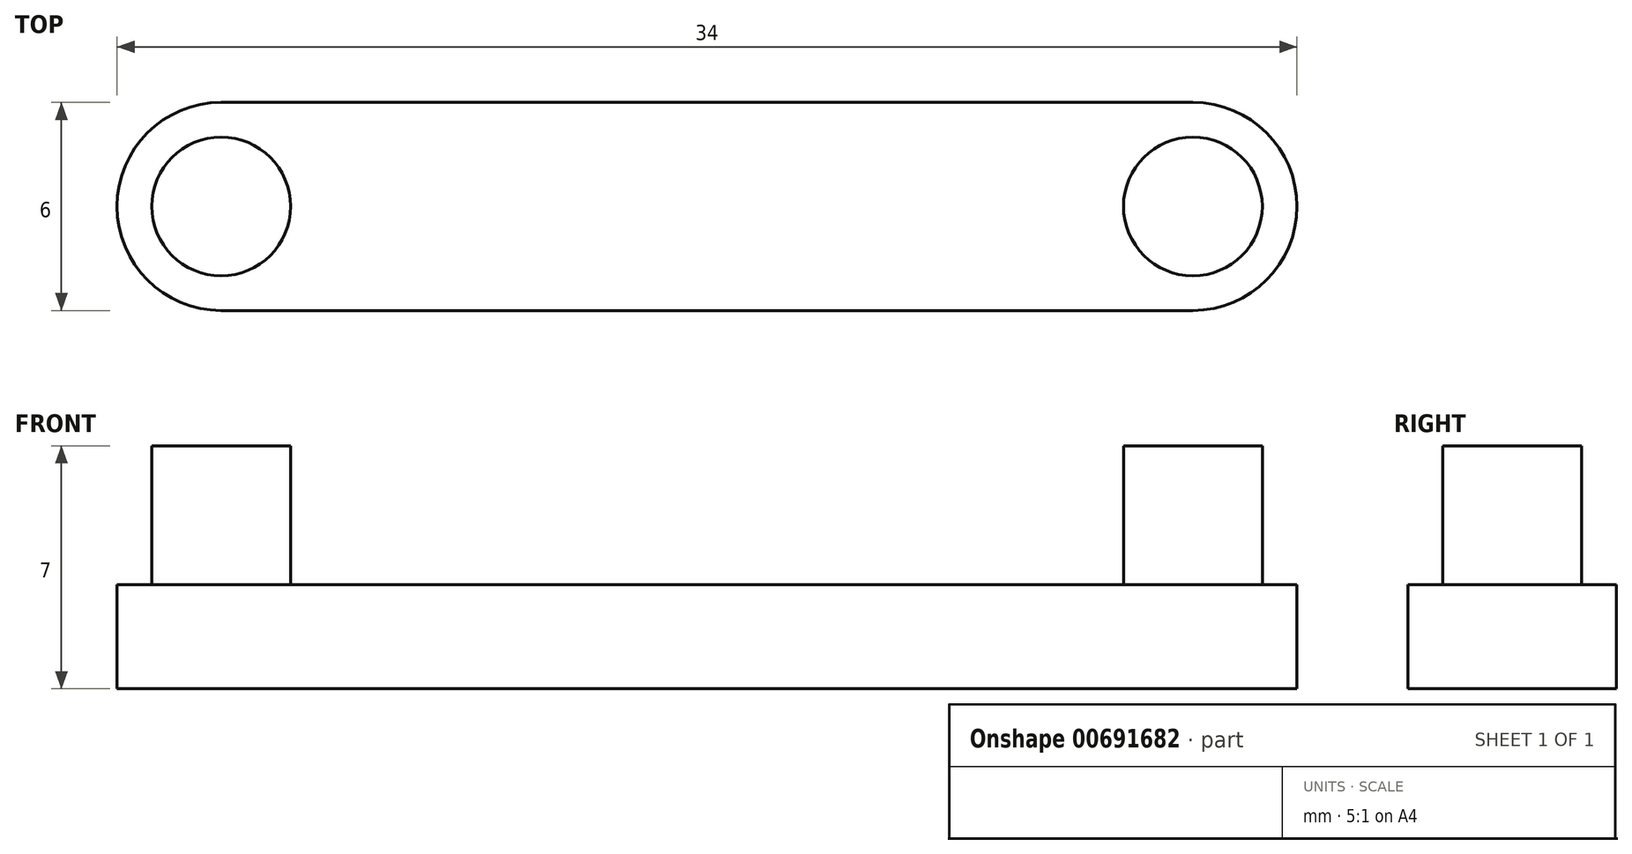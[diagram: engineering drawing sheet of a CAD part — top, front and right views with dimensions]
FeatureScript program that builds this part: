
annotation { "Feature Type Name" : "Feature", "Feature Type Description" : "" }
export const myFeature = defineFeature(function(context is Context, id is Id, definition is map)
    precondition{}
    {
        {
            var Q0;
            Q0=qCreatedBy(makeId("Top.planeOp"),FACE);
            var sketch = newSketch(context, id + "F0", { "sketchPlane" : qUnion([Q0])});
            skLineSegment(sketch, "E0.bottom", {"start": v(2, 3) * mm, "end": v(-2, 3) * mm});
            skLineSegment(sketch, "E0.top", {"start": v(2, -3) * mm, "end": v(-2, -3) * mm});
            skLineSegment(sketch, "E0.left", {"start": v(2, 3) * mm, "end": v(2, -3) * mm});
            skLineSegment(sketch, "E0.right", {"start": v(-2, 3) * mm, "end": v(-2, -3) * mm});
            skPoint(sketch, "E0.middle", {"position": v(0, 0) * mm});
            skLineSegment(sketch, "E1.bottom", {"start": v(2, 3) * mm, "end": v(14, 3) * mm});
            skLineSegment(sketch, "E1.top", {"start": v(2, -3) * mm, "end": v(14, -3) * mm});
            skLineSegment(sketch, "E1.right", {"start": v(14, 3) * mm, "end": v(14, -3) * mm});
            skLineSegment(sketch, "E2.bottom", {"start": v(-2, 3) * mm, "end": v(-14, 3) * mm});
            skLineSegment(sketch, "E2.top", {"start": v(-2, -3) * mm, "end": v(-14, -3) * mm});
            skLineSegment(sketch, "E2.right", {"start": v(-14, 3) * mm, "end": v(-14, -3) * mm});
            skCircle(sketch, "E3", {"center": v(14, 0) * mm, "radius": 3 * mm});
            skCircle(sketch, "E4", {"center": v(-14, 0) * mm, "radius": 3 * mm});
            skCircle(sketch, "E5", {"center": v(-14, 0) * mm, "radius": 2 * mm});
            skCircle(sketch, "E6", {"center": v(14, 0) * mm, "radius": 2 * mm});
            skSolve(sketch);
        }
        {
            var Q0;
            Q0 = qSketchRegion(id + "F0", true);
            extrude(context, id + "F1", {"entities" : qUnion([Q0]), "depth" : 3 * mm, "offsetDistance" : 25 * mm});
        }
        {
            var Q0;
            {var subQ0=sQuery(id+"F0.wireOp",EDGE,"E6");var subQ1=sQuery(id+"F0.wireOp",EDGE,"E1.right");var subQ2=makeQuery(id+"F0.imprint","INTERSECT",VERTEX,{"disambiguationData":[OD(0.0)],"derivedFrom":[subQ1,subQ0]});Q0=makeQuery(id+"F0.imprint","IMPRINT",FACE,{"disambiguationData":[TD([[makeQuery(id+"F0.imprint","IMPRINT",EDGE,{"disambiguationData":[TD([[subQ2,-1.0]])],"derivedFrom":subQ1}),-1.0]])]});}
            var Q1;
            {var subQ0=sQuery(id+"F0.wireOp",EDGE,"E6");var subQ1=sQuery(id+"F0.wireOp",EDGE,"E1.right");var subQ2=makeQuery(id+"F0.imprint","INTERSECT",VERTEX,{"disambiguationData":[OD(0.0)],"derivedFrom":[subQ1,subQ0]});Q1=makeQuery(id+"F0.imprint","IMPRINT",FACE,{"disambiguationData":[TD([[makeQuery(id+"F0.imprint","IMPRINT",EDGE,{"disambiguationData":[TD([[subQ2,-1.0]])],"derivedFrom":subQ1}),1.0]])]});}
            var Q2;
            {var subQ0=sQuery(id+"F0.wireOp",EDGE,"E5");var subQ1=sQuery(id+"F0.wireOp",EDGE,"E2.right");var subQ2=makeQuery(id+"F0.imprint","INTERSECT",VERTEX,{"disambiguationData":[OD(0.0)],"derivedFrom":[subQ1,subQ0]});Q2=makeQuery(id+"F0.imprint","IMPRINT",FACE,{"disambiguationData":[TD([[makeQuery(id+"F0.imprint","IMPRINT",EDGE,{"disambiguationData":[TD([[subQ2,-1.0]])],"derivedFrom":subQ1}),1.0]])]});}
            var Q3;
            {var subQ0=sQuery(id+"F0.wireOp",EDGE,"E5");var subQ1=sQuery(id+"F0.wireOp",EDGE,"E2.right");var subQ2=makeQuery(id+"F0.imprint","INTERSECT",VERTEX,{"disambiguationData":[OD(0.0)],"derivedFrom":[subQ1,subQ0]});Q3=makeQuery(id+"F0.imprint","IMPRINT",FACE,{"disambiguationData":[TD([[makeQuery(id+"F0.imprint","IMPRINT",EDGE,{"disambiguationData":[TD([[subQ2,-1.0]])],"derivedFrom":subQ1}),-1.0]])]});}
            extrude(context, id + "F2", {"entities" : qUnion([Q0, Q1, Q2, Q3]), "operationType" : NewBodyOperationType.ADD, "depth" : 7 * mm, "offsetDistance" : 25 * mm});
        }
    });
